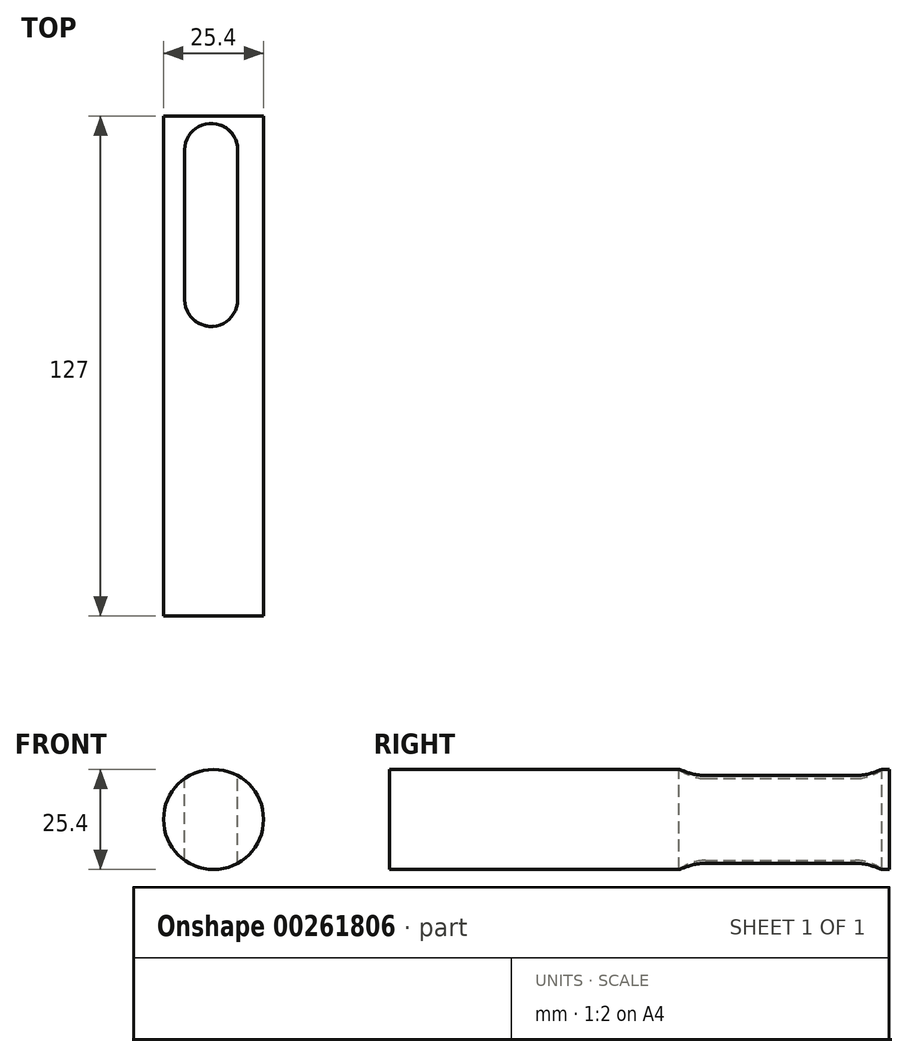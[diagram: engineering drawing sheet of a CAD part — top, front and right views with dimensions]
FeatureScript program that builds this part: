
annotation { "Feature Type Name" : "Feature", "Feature Type Description" : "" }
export const myFeature = defineFeature(function(context is Context, id is Id, definition is map)
    precondition{}
    {
        {
            var Q0;
            Q0=qCreatedBy(makeId("Front.planeOp"),FACE);
            var sketch = newSketch(context, id + "F0", { "sketchPlane" : qUnion([Q0])});
            skCircle(sketch, "E0", {"center": v(0, 0) * mm, "radius": 12.7 * mm});
            skSolve(sketch);
        }
        {
            var Q0;
            Q0 = qSketchRegion(id + "F0", true);
            extrude(context, id + "F1", {"entities" : qUnion([Q0]), "depth" : 127 * mm});
        }
        {
            var Q0;
            Q0=qCreatedBy(makeId("Top.planeOp"),FACE);
            var sketch = newSketch(context, id + "F2", { "sketchPlane" : qUnion([Q0])});
            skLineSegment(sketch, "E1", {"start": v(-7.31, -8.57) * mm, "end": v(-7.31, -46.7) * mm});
            skLineSegment(sketch, "E2", {"start": v(6.12, -8.57) * mm, "end": v(6.12, -46.7) * mm});
            skArc(sketch, "E3", {"start": v(-7.31, -46.7) * mm, "mid": v(-0.6, -53.43) * mm, "end": v(6.12, -46.7) * mm});
            skArc(sketch, "E4", {"start": v(6.12, -8.57) * mm, "mid": v(-0.6, -1.85) * mm, "end": v(-7.31, -8.57) * mm});
            skSolve(sketch);
        }
        {
            var Q0;
            Q0 = qSketchRegion(id + "F2", true);
            extrude(context, id + "F3", {"entities" : qUnion([Q0]), "operationType" : NewBodyOperationType.REMOVE, "endBound" : BoundingType.SYMMETRIC, "oppositeDirection" : true, "depth" : 25.4 * mm});
        }
    });
